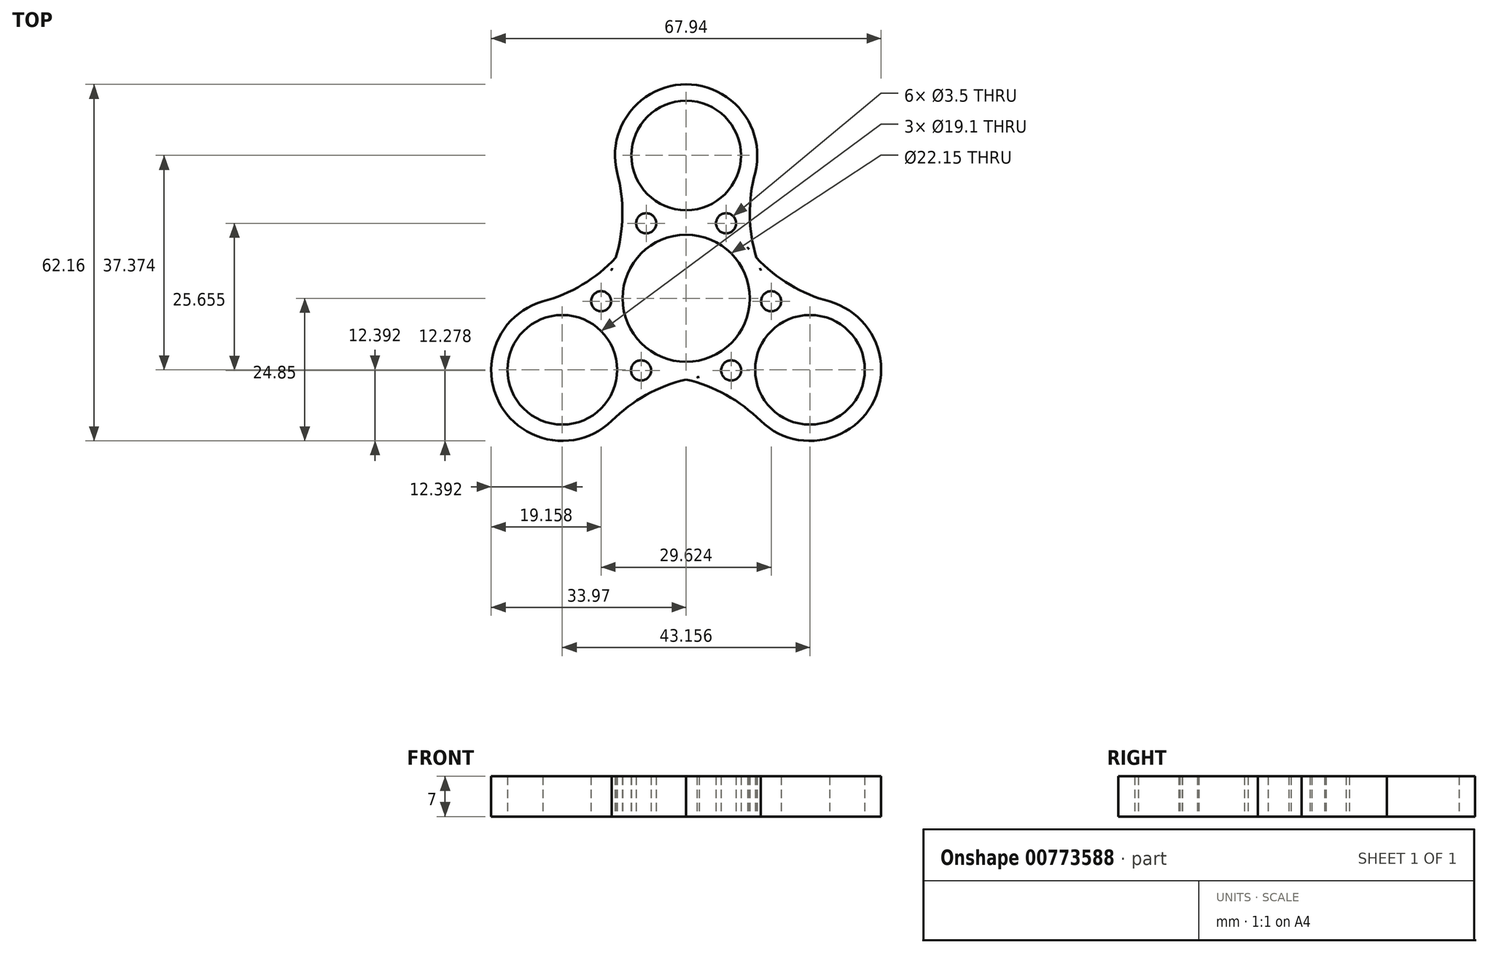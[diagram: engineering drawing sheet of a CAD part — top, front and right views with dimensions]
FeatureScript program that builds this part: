
annotation { "Feature Type Name" : "Feature", "Feature Type Description" : "" }
export const myFeature = defineFeature(function(context is Context, id is Id, definition is map)
    precondition{}
    {
        {
            var Q0;
            Q0=qCreatedBy(makeId("Top.planeOp"),FACE);
            var sketch = newSketch(context, id + "F0", { "sketchPlane" : qUnion([Q0])});
            skCircle(sketch, "E0", {"center": v(0, 0) * mm, "radius": 11.07 * mm});
            skCircle(sketch, "E1", {"center": v(0, 24.92) * mm, "radius": 9.55 * mm});
            skArc(sketch, "E2", {"start": v(11.95, 21.62) * mm, "mid": v(0, 37.3) * mm, "end": v(-11.95, 21.62) * mm});
            skArc(sketch, "E3", {"start": v(-13.02, 4.86) * mm, "mid": v(-12.95, 5.05) * mm, "end": v(-12.88, 5.24) * mm});
            skArc(sketch, "E4.MirrorCS", {"start": v(13.02, 4.86) * mm, "mid": v(12.95, 5.05) * mm, "end": v(12.88, 5.24) * mm});
            skCircle(sketch, "E5.1.0", {"center": v(-21.58, -12.46) * mm, "radius": 9.55 * mm});
            skArc(sketch, "E5.1.1", {"start": v(-24.7, -0.47) * mm, "mid": v(-32.3, -18.65) * mm, "end": v(-12.75, -21.16) * mm});
            skArc(sketch, "E5.1.2", {"start": v(2.3, -13.7) * mm, "mid": v(2.1, -13.74) * mm, "end": v(1.9, -13.77) * mm});
            skArc(sketch, "E5.1.3", {"start": v(-10.72, 8.85) * mm, "mid": v(-10.85, 8.69) * mm, "end": v(-10.97, 8.53) * mm});
            skCircle(sketch, "E5.2.0", {"center": v(21.58, -12.46) * mm, "radius": 9.55 * mm});
            skArc(sketch, "E5.2.1", {"start": v(12.75, -21.16) * mm, "mid": v(32.3, -18.65) * mm, "end": v(24.7, -0.47) * mm});
            skArc(sketch, "E5.2.2", {"start": v(10.72, 8.85) * mm, "mid": v(10.85, 8.69) * mm, "end": v(10.97, 8.53) * mm});
            skArc(sketch, "E6.trimOffspring", {"start": v(1.9, -13.77) * mm, "mid": v(2.1, -13.74) * mm, "end": v(2.3, -13.7) * mm});
            skArc(sketch, "E7.trimOffspring", {"start": v(0, -14.14) * mm, "mid": v(7, -16.85) * mm, "end": v(12.97, -21.37) * mm});
            skArc(sketch, "E8.trimOffspring", {"start": v(0, -14.14) * mm, "mid": v(-7, -16.85) * mm, "end": v(-12.97, -21.37) * mm});
            skArc(sketch, "E9.trimOffspring", {"start": v(-12.88, 5.24) * mm, "mid": v(-12.95, 5.05) * mm, "end": v(-13.02, 4.86) * mm});
            skArc(sketch, "E10.trimOffspring", {"start": v(-12.25, 7.07) * mm, "mid": v(-11.1, 14.48) * mm, "end": v(-12.02, 21.92) * mm});
            skArc(sketch, "E11.trimOffspring", {"start": v(-12.25, 7.07) * mm, "mid": v(-18.1, 2.37) * mm, "end": v(-25, -0.55) * mm});
            skArc(sketch, "E12.trimOffspring", {"start": v(10.97, 8.53) * mm, "mid": v(10.85, 8.69) * mm, "end": v(10.72, 8.85) * mm});
            skArc(sketch, "E13.trimOffspring", {"start": v(12.25, 7.07) * mm, "mid": v(11.1, 14.48) * mm, "end": v(12.02, 21.92) * mm});
            skArc(sketch, "E14.trimOffspring", {"start": v(12.25, 7.07) * mm, "mid": v(18.1, 2.37) * mm, "end": v(25, -0.55) * mm});
            skCircle(sketch, "E15", {"center": v(-7.85, -12.57) * mm, "radius": 1.75 * mm});
            skLineSegment(sketch, "E16", {"start": v(-5.83, -9.42) * mm, "end": v(-6.83, -11.15) * mm, "construction": true});
            skCircle(sketch, "E17.1.0", {"center": v(14.81, -0.51) * mm, "radius": 1.75 * mm});
            skCircle(sketch, "E17.2.0", {"center": v(-6.96, 13.08) * mm, "radius": 1.75 * mm});
            skCircle(sketch, "E18.MirrorC", {"center": v(7.85, -12.57) * mm, "radius": 1.75 * mm});
            skCircle(sketch, "E19.1.0", {"center": v(6.96, 13.08) * mm, "radius": 1.75 * mm});
            skCircle(sketch, "E19.2.0", {"center": v(-14.81, -0.51) * mm, "radius": 1.75 * mm});
            skSolve(sketch);
        }
        {
            var Q0;
            Q0=makeQuery(id+"F0.imprint","IMPRINT",FACE,{"disambiguationData":[TD([[makeQuery(id+"F0.imprint","IMPRINT",EDGE,{"derivedFrom":sQuery(id+"F0.wireOp",EDGE,"E0")}),-1.0]])]});
            extrude(context, id + "F1", {"entities" : qUnion([Q0]), "depth" : 7 * mm, "offsetDistance" : 25 * mm});
        }
    });
